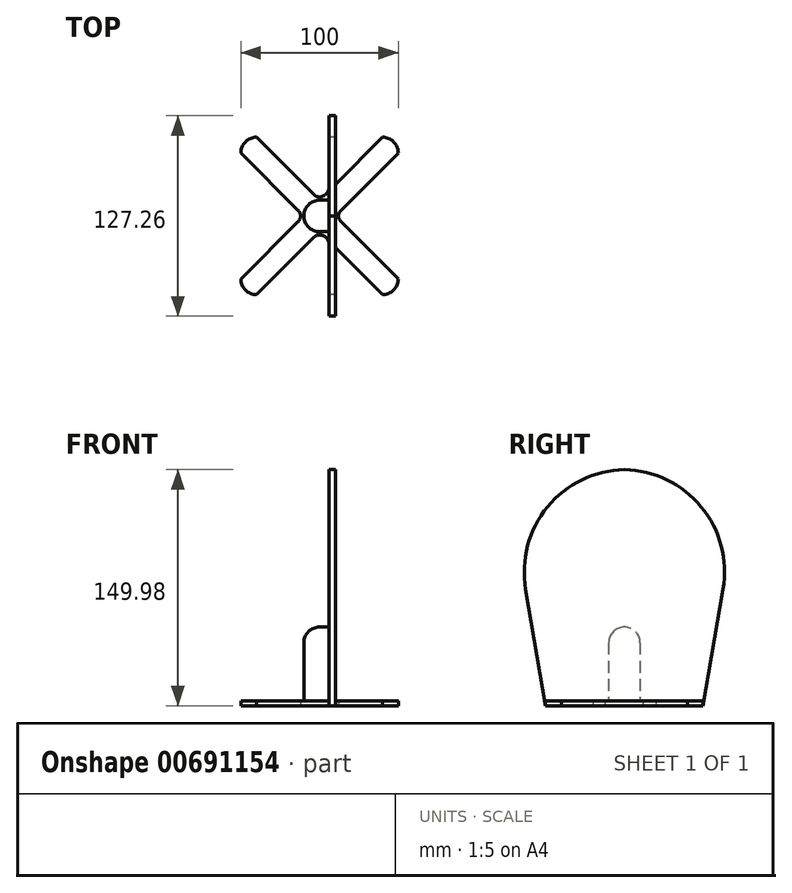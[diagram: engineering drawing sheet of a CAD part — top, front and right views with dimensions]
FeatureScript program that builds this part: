
annotation { "Feature Type Name" : "Feature", "Feature Type Description" : "" }
export const myFeature = defineFeature(function(context is Context, id is Id, definition is map)
    precondition{}
    {
        {
            var Q0;
            Q0=qCreatedBy(makeId("Top.planeOp"),FACE);
            var sketch = newSketch(context, id + "F0", { "sketchPlane" : qUnion([Q0])});
            skCircle(sketch, "E0", {"center": v(0, 0) * mm, "radius": 10 * mm});
            skLineSegment(sketch, "E1.bottom", {"start": v(-50, 50) * mm, "end": v(50, 50) * mm});
            skLineSegment(sketch, "E1.top", {"start": v(-50, -50) * mm, "end": v(50, -50) * mm});
            skLineSegment(sketch, "E1.left", {"start": v(-50, 50) * mm, "end": v(-50, -50) * mm});
            skLineSegment(sketch, "E1.right", {"start": v(50, 50) * mm, "end": v(50, -50) * mm});
            skLineSegment(sketch, "E2", {"start": v(-50, 50) * mm, "end": v(-40, 50) * mm});
            skLineSegment(sketch, "E3", {"start": v(50, -50) * mm, "end": v(50, -40) * mm});
            skLineSegment(sketch, "E4", {"start": v(-40, 50) * mm, "end": v(50, -40) * mm});
            skLineSegment(sketch, "E5", {"start": v(-50, 50) * mm, "end": v(-50, 40) * mm});
            skLineSegment(sketch, "E6", {"start": v(-50, -50) * mm, "end": v(-50, -40) * mm});
            skLineSegment(sketch, "E7", {"start": v(-50, -50) * mm, "end": v(-40, -50) * mm});
            skLineSegment(sketch, "E8", {"start": v(50, -50) * mm, "end": v(40, -50) * mm});
            skLineSegment(sketch, "E9", {"start": v(50, 50) * mm, "end": v(50, 40) * mm});
            skLineSegment(sketch, "E10", {"start": v(50, 50) * mm, "end": v(40, 50) * mm});
            skLineSegment(sketch, "E11", {"start": v(-50, 40) * mm, "end": v(40, -50) * mm});
            skLineSegment(sketch, "E12", {"start": v(-50, -40) * mm, "end": v(40, 50) * mm});
            skLineSegment(sketch, "E13", {"start": v(-40, -50) * mm, "end": v(50, 40) * mm});
            skSolve(sketch);
        }
        {
            var Q0;
            {var subQ0=sQuery(id+"F0.wireOp",EDGE,"E4");var subQ1=sQuery(id+"F0.wireOp",EDGE,"E1.bottom");var subQ2=makeQuery(id+"F0.imprint","INTERSECT",VERTEX,{"derivedFrom":[subQ1,subQ0]});Q0=makeQuery(id+"F0.imprint","IMPRINT",FACE,{"disambiguationData":[TD([[makeQuery(id+"F0.imprint","IMPRINT",EDGE,{"disambiguationData":[TD([[subQ2,1.0]])],"derivedFrom":subQ1}),-1.0]])]});}
            var Q1;
            {var subQ0=sQuery(id+"F0.wireOp",EDGE,"E12");var subQ1=sQuery(id+"F0.wireOp",EDGE,"E0");var subQ2=makeQuery(id+"F0.imprint","INTERSECT",VERTEX,{"derivedFrom":[subQ1,sQuery(id+"F0.wireOp",EDGE,"E4"),subQ0]});Q1=makeQuery(id+"F0.imprint","IMPRINT",FACE,{"disambiguationData":[TD([[makeQuery(id+"F0.imprint","IMPRINT",EDGE,{"disambiguationData":[TD([[subQ2,-1.0]])],"derivedFrom":subQ1}),1.0]])]});}
            var Q2;
            {var subQ0=sQuery(id+"F0.wireOp",EDGE,"E13");var subQ1=sQuery(id+"F0.wireOp",EDGE,"E4");var subQ2=sQuery(id+"F0.wireOp",EDGE,"E0");var subQ3=makeQuery(id+"F0.imprint","INTERSECT",VERTEX,{"derivedFrom":[subQ2,subQ1,subQ0]});Q2=makeQuery(id+"F0.imprint","IMPRINT",FACE,{"disambiguationData":[TD([[makeQuery(id+"F0.imprint","IMPRINT",EDGE,{"disambiguationData":[TD([[subQ3,1.0]])],"derivedFrom":subQ1}),-1.0]])]});}
            var Q3;
            {var subQ0=sQuery(id+"F0.wireOp",EDGE,"E13");var subQ1=sQuery(id+"F0.wireOp",EDGE,"E0");var subQ2=makeQuery(id+"F0.imprint","INTERSECT",VERTEX,{"derivedFrom":[subQ1,sQuery(id+"F0.wireOp",EDGE,"E4"),subQ0]});Q3=makeQuery(id+"F0.imprint","IMPRINT",FACE,{"disambiguationData":[TD([[makeQuery(id+"F0.imprint","IMPRINT",EDGE,{"disambiguationData":[TD([[subQ2,1.0]])],"derivedFrom":subQ1}),1.0]])]});}
            var Q4;
            {var subQ0=sQuery(id+"F0.wireOp",EDGE,"E4");var subQ1=sQuery(id+"F0.wireOp",EDGE,"E0");var subQ2=makeQuery(id+"F0.imprint","INTERSECT",VERTEX,{"derivedFrom":[subQ1,subQ0,sQuery(id+"F0.wireOp",EDGE,"E13")]});Q4=makeQuery(id+"F0.imprint","IMPRINT",FACE,{"disambiguationData":[TD([[makeQuery(id+"F0.imprint","IMPRINT",EDGE,{"disambiguationData":[TD([[subQ2,-1.0]])],"derivedFrom":subQ1}),1.0]])]});}
            var Q5;
            {var subQ0=sQuery(id+"F0.wireOp",EDGE,"E11");var subQ1=sQuery(id+"F0.wireOp",EDGE,"E0");var subQ2=makeQuery(id+"F0.imprint","INTERSECT",VERTEX,{"derivedFrom":[subQ1,subQ0,sQuery(id+"F0.wireOp",EDGE,"E13")]});Q5=makeQuery(id+"F0.imprint","IMPRINT",FACE,{"disambiguationData":[TD([[makeQuery(id+"F0.imprint","IMPRINT",EDGE,{"disambiguationData":[TD([[subQ2,1.0]])],"derivedFrom":subQ1}),1.0]])]});}
            var Q6;
            {var subQ3=sQuery(id+"F0.wireOp",EDGE,"E1.top");var subQ8=sQuery(id+"F0.wireOp",EDGE,"E13");var subQ9=makeQuery(id+"F0.imprint","INTERSECT",VERTEX,{"derivedFrom":[subQ3,subQ8]});Q6=makeQuery(id+"F0.imprint","IMPRINT",FACE,{"disambiguationData":[TD([[makeQuery(id+"F0.imprint","IMPRINT",EDGE,{"disambiguationData":[TD([[subQ9,1.0]])],"derivedFrom":subQ3}),1.0]])]});}
            var Q7;
            {var subQ4=sQuery(id+"F0.wireOp",EDGE,"E1.right");var subQ6=sQuery(id+"F0.wireOp",EDGE,"E1.top");var subQ7=makeQuery(id+"F0.imprint","INTERSECT",VERTEX,{"derivedFrom":[subQ6,subQ4]});Q7=makeQuery(id+"F0.imprint","IMPRINT",FACE,{"disambiguationData":[TD([[makeQuery(id+"F0.imprint","IMPRINT",EDGE,{"disambiguationData":[TD([[subQ7,1.0]])],"derivedFrom":subQ6}),1.0]])]});}
            var Q8;
            {var subQ4=sQuery(id+"F0.wireOp",EDGE,"E1.bottom");var subQ7=sQuery(id+"F0.wireOp",EDGE,"E1.right");var subQ9=makeQuery(id+"F0.imprint","INTERSECT",VERTEX,{"derivedFrom":[subQ4,subQ7]});Q8=makeQuery(id+"F0.imprint","IMPRINT",FACE,{"disambiguationData":[TD([[makeQuery(id+"F0.imprint","IMPRINT",EDGE,{"disambiguationData":[TD([[subQ9,1.0]])],"derivedFrom":subQ4}),-1.0]])]});}
            extrude(context, id + "F1", {"entities" : qUnion([Q0, Q1, Q2, Q3, Q4, Q5, Q6, Q7, Q8]), "depth" : 3 * mm, "offsetDistance" : 25 * mm});
        }
        {
            var Q0;
            Q0=makeQuery(id+"F1.opExtrude","SWEPT_EDGE",EDGE,{"disambiguationData":[OSD([sQuery(id+"F0.wireOp",EDGE,"E1.bottom"),sQuery(id+"F0.wireOp",EDGE,"E1.left")])]});
            var Q1;
            Q1=makeQuery(id+"F1.opExtrude","SWEPT_EDGE",EDGE,{"disambiguationData":[OSD([sQuery(id+"F0.wireOp",EDGE,"E1.top"),sQuery(id+"F0.wireOp",EDGE,"E1.left")])]});
            var Q2;
            Q2=makeQuery(id+"F1.opExtrude","SWEPT_EDGE",EDGE,{"disambiguationData":[OSD([sQuery(id+"F0.wireOp",EDGE,"E1.top"),sQuery(id+"F0.wireOp",EDGE,"E1.right")])]});
            var Q3;
            Q3=makeQuery(id+"F1.opExtrude","SWEPT_EDGE",EDGE,{"disambiguationData":[OSD([sQuery(id+"F0.wireOp",EDGE,"E1.bottom"),sQuery(id+"F0.wireOp",EDGE,"E1.right")])]});
            fillet(context, id + "F2", {"entities" : qUnion([Q0, Q1, Q2, Q3]), "radius" : 10 * mm, "tangentPropagation" : true, "allowEdgeOverflow" : false});
        }
        {
            var Q0;
            Q0=makeQuery(id+"F1.opExtrude","SWEPT_EDGE",EDGE,{"disambiguationData":[OSD([sQuery(id+"F0.wireOp",EDGE,"E0"),sQuery(id+"F0.wireOp",EDGE,"E4"),sQuery(id+"F0.wireOp",EDGE,"E13")])]});
            var Q1;
            Q1=makeQuery(id+"F1.opExtrude","SWEPT_EDGE",EDGE,{"disambiguationData":[OSD([sQuery(id+"F0.wireOp",EDGE,"E0"),sQuery(id+"F0.wireOp",EDGE,"E4"),sQuery(id+"F0.wireOp",EDGE,"E12")])]});
            var Q2;
            Q2=makeQuery(id+"F1.opExtrude","SWEPT_EDGE",EDGE,{"disambiguationData":[OSD([sQuery(id+"F0.wireOp",EDGE,"E0"),sQuery(id+"F0.wireOp",EDGE,"E11"),sQuery(id+"F0.wireOp",EDGE,"E12")])]});
            var Q3;
            Q3=makeQuery(id+"F1.opExtrude","SWEPT_EDGE",EDGE,{"disambiguationData":[OSD([sQuery(id+"F0.wireOp",EDGE,"E0"),sQuery(id+"F0.wireOp",EDGE,"E11"),sQuery(id+"F0.wireOp",EDGE,"E13")])]});
            fillet(context, id + "F3", {"entities" : qUnion([Q0, Q1, Q2, Q3]), "radius" : 5 * mm, "tangentPropagation" : true, "allowEdgeOverflow" : false});
        }
        {
            var Q0;
            {var subQ0=sQuery(id+"F0.wireOp",EDGE,"E13");var subQ1=sQuery(id+"F0.wireOp",EDGE,"E4");var subQ2=sQuery(id+"F0.wireOp",EDGE,"E0");var subQ3=makeQuery(id+"F0.imprint","INTERSECT",VERTEX,{"derivedFrom":[subQ2,subQ1,subQ0]});Q0=makeQuery(id+"F0.imprint","IMPRINT",FACE,{"disambiguationData":[TD([[makeQuery(id+"F0.imprint","IMPRINT",EDGE,{"disambiguationData":[TD([[subQ3,1.0]])],"derivedFrom":subQ1}),-1.0]])]});}
            var Q1;
            {var subQ0=sQuery(id+"F0.wireOp",EDGE,"E13");var subQ1=sQuery(id+"F0.wireOp",EDGE,"E0");var subQ2=makeQuery(id+"F0.imprint","INTERSECT",VERTEX,{"derivedFrom":[subQ1,sQuery(id+"F0.wireOp",EDGE,"E4"),subQ0]});Q1=makeQuery(id+"F0.imprint","IMPRINT",FACE,{"disambiguationData":[TD([[makeQuery(id+"F0.imprint","IMPRINT",EDGE,{"disambiguationData":[TD([[subQ2,1.0]])],"derivedFrom":subQ1}),1.0]])]});}
            var Q2;
            {var subQ0=sQuery(id+"F0.wireOp",EDGE,"E4");var subQ1=sQuery(id+"F0.wireOp",EDGE,"E0");var subQ2=makeQuery(id+"F0.imprint","INTERSECT",VERTEX,{"derivedFrom":[subQ1,subQ0,sQuery(id+"F0.wireOp",EDGE,"E13")]});Q2=makeQuery(id+"F0.imprint","IMPRINT",FACE,{"disambiguationData":[TD([[makeQuery(id+"F0.imprint","IMPRINT",EDGE,{"disambiguationData":[TD([[subQ2,-1.0]])],"derivedFrom":subQ1}),1.0]])]});}
            var Q3;
            {var subQ0=sQuery(id+"F0.wireOp",EDGE,"E12");var subQ1=sQuery(id+"F0.wireOp",EDGE,"E0");var subQ2=makeQuery(id+"F0.imprint","INTERSECT",VERTEX,{"derivedFrom":[subQ1,sQuery(id+"F0.wireOp",EDGE,"E4"),subQ0]});Q3=makeQuery(id+"F0.imprint","IMPRINT",FACE,{"disambiguationData":[TD([[makeQuery(id+"F0.imprint","IMPRINT",EDGE,{"disambiguationData":[TD([[subQ2,-1.0]])],"derivedFrom":subQ1}),1.0]])]});}
            var Q4;
            {var subQ0=sQuery(id+"F0.wireOp",EDGE,"E11");var subQ1=sQuery(id+"F0.wireOp",EDGE,"E0");var subQ2=makeQuery(id+"F0.imprint","INTERSECT",VERTEX,{"derivedFrom":[subQ1,subQ0,sQuery(id+"F0.wireOp",EDGE,"E13")]});Q4=makeQuery(id+"F0.imprint","IMPRINT",FACE,{"disambiguationData":[TD([[makeQuery(id+"F0.imprint","IMPRINT",EDGE,{"disambiguationData":[TD([[subQ2,1.0]])],"derivedFrom":subQ1}),1.0]])]});}
            extrude(context, id + "F4", {"entities" : qUnion([Q0, Q1, Q2, Q3, Q4]), "operationType" : NewBodyOperationType.ADD, "depth" : 50 * mm, "offsetDistance" : 25 * mm});
        }
        {
            var Q0;
            Q0=qCreatedBy(makeId("Right.planeOp"),FACE);
            var sketch = newSketch(context, id + "F5", { "sketchPlane" : qUnion([Q0])});
            skLineSegment(sketch, "E14", {"start": v(0, 0) * mm, "end": v(0, -50) * mm});
            skLineSegment(sketch, "E15", {"start": v(0, 0) * mm, "end": v(0, 150) * mm});
            skCircle(sketch, "E16", {"center": v(0, -50) * mm, "radius": 200 * mm});
            skLineSegment(sketch, "E17", {"start": v(0, 0) * mm, "end": v(-50, 0) * mm});
            skLineSegment(sketch, "E18", {"start": v(0, 0) * mm, "end": v(50, 0) * mm});
            skLineSegment(sketch, "E19", {"start": v(0, -50) * mm, "end": v(-200, -50) * mm});
            skLineSegment(sketch, "E20", {"start": v(-200, -50) * mm, "end": v(200, -50) * mm});
            skLineSegment(sketch, "E21", {"start": v(200, -50) * mm, "end": v(0, 150) * mm});
            skLineSegment(sketch, "E22", {"start": v(-200, -50) * mm, "end": v(0, 150) * mm});
            skLineSegment(sketch, "E23", {"start": v(0, -50) * mm, "end": v(-100, 50) * mm});
            skLineSegment(sketch, "E24", {"start": v(-100, 50) * mm, "end": v(-141.42, 91.42) * mm});
            skLineSegment(sketch, "E25", {"start": v(-141.42, 91.42) * mm, "end": v(0, 150) * mm});
            skLineSegment(sketch, "E26", {"start": v(0, -50) * mm, "end": v(100, 50) * mm});
            skLineSegment(sketch, "E27", {"start": v(100, 50) * mm, "end": v(141.42, 91.42) * mm});
            skLineSegment(sketch, "E28", {"start": v(141.42, 91.42) * mm, "end": v(0, 150) * mm});
            skLineSegment(sketch, "E29", {"start": v(-70.71, 120.71) * mm, "end": v(-50, 0) * mm});
            skLineSegment(sketch, "E30", {"start": v(50, 0) * mm, "end": v(70.71, 120.71) * mm});
            skLineSegment(sketch, "E31", {"start": v(-50, 0) * mm, "end": v(-73.35, 136.07) * mm});
            skLineSegment(sketch, "E32", {"start": v(50, 0) * mm, "end": v(73.35, 136.07) * mm});
            skSolve(sketch);
        }
        {
            var Q0;
            {var subQ3=sQuery(id+"F5.wireOp",EDGE,"E31");Q0=makeQuery(id+"F5.imprint","IMPRINT",FACE,{"disambiguationData":[TD([[makeQuery(id+"F5.imprint","IMPRINT",EDGE,{"derivedFrom":subQ3}),-1.0]])]});}
            var Q1;
            {var subQ1=sQuery(id+"F5.wireOp",EDGE,"E22");var subQ3=sQuery(id+"F5.wireOp",EDGE,"E29");var subQ4=makeQuery(id+"F5.imprint","INTERSECT",VERTEX,{"derivedFrom":[subQ1,subQ3]});Q1=makeQuery(id+"F5.imprint","IMPRINT",FACE,{"disambiguationData":[TD([[makeQuery(id+"F5.imprint","IMPRINT",EDGE,{"disambiguationData":[TD([[subQ4,1.0]])],"derivedFrom":subQ3}),1.0]])]});}
            var Q2;
            {var subQ0=sQuery(id+"F5.wireOp",EDGE,"E15");Q2=makeQuery(id+"F5.imprint","IMPRINT",FACE,{"disambiguationData":[TD([[makeQuery(id+"F5.imprint","IMPRINT",EDGE,{"derivedFrom":subQ0}),1.0]])]});}
            var Q3;
            {var subQ0=sQuery(id+"F5.wireOp",EDGE,"E15");Q3=makeQuery(id+"F5.imprint","IMPRINT",FACE,{"disambiguationData":[TD([[makeQuery(id+"F5.imprint","IMPRINT",EDGE,{"derivedFrom":subQ0}),-1.0]])]});}
            var Q4;
            {var subQ1=sQuery(id+"F5.wireOp",EDGE,"E21");var subQ3=sQuery(id+"F5.wireOp",EDGE,"E30");var subQ4=makeQuery(id+"F5.imprint","INTERSECT",VERTEX,{"derivedFrom":[subQ1,subQ3]});Q4=makeQuery(id+"F5.imprint","IMPRINT",FACE,{"disambiguationData":[TD([[makeQuery(id+"F5.imprint","IMPRINT",EDGE,{"disambiguationData":[TD([[subQ4,-1.0]])],"derivedFrom":subQ3}),1.0]])]});}
            var Q5;
            {var subQ3=sQuery(id+"F5.wireOp",EDGE,"E32");Q5=makeQuery(id+"F5.imprint","IMPRINT",FACE,{"disambiguationData":[TD([[makeQuery(id+"F5.imprint","IMPRINT",EDGE,{"derivedFrom":subQ3}),1.0]])]});}
            extrude(context, id + "F6", {"entities" : qUnion([Q0, Q1, Q2, Q3, Q4, Q5]), "operationType" : NewBodyOperationType.ADD, "depth" : 10 * mm, "offsetDistance" : 25 * mm});
        }
        {
            var Q0;
            Q0=makeQuery(id+"F6.opExtrude","CAP_FACE",FACE,{"disambiguationData":[OSD([sQuery(id+"F5.wireOp",EDGE,"E16"),sQuery(id+"F5.wireOp",EDGE,"E17"),sQuery(id+"F5.wireOp",EDGE,"E18"),sQuery(id+"F5.wireOp",EDGE,"E29"),sQuery(id+"F5.wireOp",EDGE,"E30"),sQuery(id+"F5.wireOp",EDGE,"E31"),sQuery(id+"F5.wireOp",EDGE,"E32")])],"isStart":true});
            extrude(context, id + "F7", {"entities" : qUnion([Q0]), "operationType" : NewBodyOperationType.REMOVE, "oppositeDirection" : true, "depth" : 6 * mm, "offsetDistance" : 25 * mm});
        }
        {
            var Q0;
            Q0=makeQuery(id+"F6.opExtrude","SWEPT_EDGE",EDGE,{"disambiguationData":[OSD([sQuery(id+"F5.wireOp",EDGE,"E16"),sQuery(id+"F5.wireOp",EDGE,"E31")])]});
            var Q1;
            Q1=makeQuery(id+"F6.opExtrude","SWEPT_EDGE",EDGE,{"disambiguationData":[OSD([sQuery(id+"F5.wireOp",EDGE,"E16"),sQuery(id+"F5.wireOp",EDGE,"E32")])]});
            fillet(context, id + "F8", {"entities" : qUnion([Q0, Q1]), "radius" : 65 * mm, "tangentPropagation" : true, "allowEdgeOverflow" : false});
        }
        {
            var Q0;
            Q0=makeQuery(id+"F4.opExtrude","CAP_EDGE",EDGE,{"disambiguationData":[OSD([sQuery(id+"F0.wireOp",EDGE,"E0")])],"isStart":false});
            fillet(context, id + "F9", {"entities" : qUnion([Q0]), "radius" : 10 * mm, "tangentPropagation" : true, "allowEdgeOverflow" : false});
        }
        {
            var Q0;
            Q0=makeQuery(id+"F7.boolean.opBoolean","COPY",EDGE,{"derivedFrom":makeQuery(id+"F7.opExtrude","CAP_EDGE",EDGE,{"disambiguationData":[OSD([sQuery(id+"F0.wireOp",EDGE,"E0"),sQuery(id+"F0.wireOp",EDGE,"E4"),sQuery(id+"F0.wireOp",EDGE,"E12"),sQuery(id+"F5.wireOp",EDGE,"E16"),sQuery(id+"F5.wireOp",EDGE,"E17"),sQuery(id+"F5.wireOp",EDGE,"E18"),sQuery(id+"F5.wireOp",EDGE,"E29"),sQuery(id+"F5.wireOp",EDGE,"E30"),sQuery(id+"F5.wireOp",EDGE,"E31"),sQuery(id+"F5.wireOp",EDGE,"E32")])],"isStart":false})});
            var Q1;
            Q1=makeQuery(id+"F7.boolean.opBoolean","COPY",EDGE,{"derivedFrom":makeQuery(id+"F7.opExtrude","CAP_EDGE",EDGE,{"disambiguationData":[OSD([sQuery(id+"F0.wireOp",EDGE,"E0"),sQuery(id+"F0.wireOp",EDGE,"E11"),sQuery(id+"F0.wireOp",EDGE,"E13"),sQuery(id+"F5.wireOp",EDGE,"E16"),sQuery(id+"F5.wireOp",EDGE,"E17"),sQuery(id+"F5.wireOp",EDGE,"E18"),sQuery(id+"F5.wireOp",EDGE,"E29"),sQuery(id+"F5.wireOp",EDGE,"E30"),sQuery(id+"F5.wireOp",EDGE,"E31"),sQuery(id+"F5.wireOp",EDGE,"E32")])],"isStart":false})});
            fillet(context, id + "F10", {"entities" : qUnion([Q0, Q1]), "radius" : 6 * mm, "tangentPropagation" : true, "allowEdgeOverflow" : false});
        }
    });
